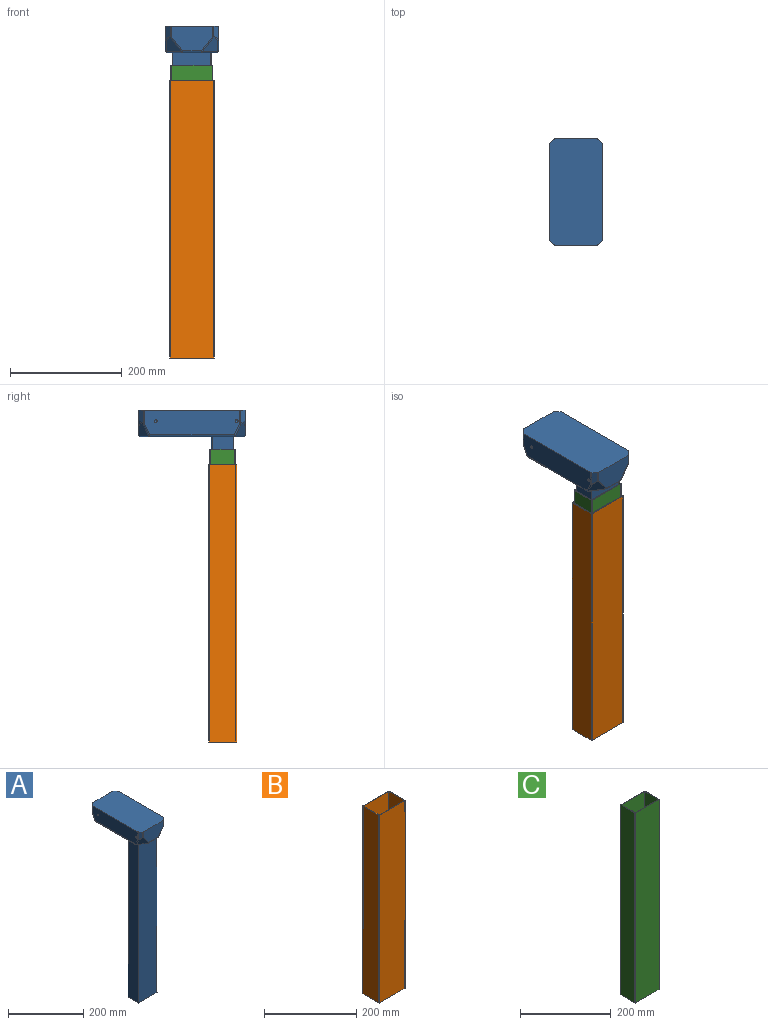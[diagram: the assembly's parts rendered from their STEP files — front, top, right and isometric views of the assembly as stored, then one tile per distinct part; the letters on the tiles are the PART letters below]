
ASSEMBLY  parts=3 mates=2
PART A: 90 faces, bbox 95.3x190.5x569.1 mm
  f0: plane 521.49x67.79mm, normal (0,1,0), area 35353mm2, adj f1,f13,f14,f79
  f1: cylinder r=1.27mm len=521.49mm, axis (0,0,-1), area 1040.3mm2, adj f0,f2,f14,f79
  f2: plane 521.49x39.09mm, normal (-1,0,0), area 20385.3mm2, adj f1,f3,f14,f79
  f3: plane 521.49x69.06mm, normal (0,-1,0), area 36015.3mm2, adj f2,f4,f14,f79
  f4: cylinder r=1.27mm len=521.49mm, axis (0,0,-1), area 1040.3mm2, adj f3,f5,f14,f79
  f5: plane 521.49x37.82mm, normal (1,0,0), area 19723mm2, adj f4,f13,f14,f79
  f6: cylinder r=0.13mm len=521.49mm, axis (0,0,-1), area 104mm2, adj f7,f12,f14,f81
  f7: plane 521.49x66.93mm, normal (0,-1,0), area 34902.6mm2, adj f6,f8,f14,f81
  f8: cylinder r=0.13mm len=521.49mm, axis (0,0,-1), area 104mm2, adj f7,f9,f14,f81
  f9: plane 521.49x36.96mm, normal (-1,0,0), area 19272.6mm2, adj f8,f10,f14,f81
  f10: cylinder r=0.13mm len=521.49mm, axis (0,0,-1), area 104mm2, adj f9,f11,f14,f81
  f11: plane 521.49x67.06mm, normal (0,1,0), area 34968.9mm2, adj f10,f12,f14,f81
  f12: plane 521.49x37.08mm, normal (1,0,0), area 19338.8mm2, adj f6,f11,f14,f81
  f13: cylinder r=1.27mm len=521.49mm, axis (0,0,-1), area 1040.3mm2, adj f0,f5,f14,f79
  f14: plane 70.33x40.36mm, normal (0,0,-1), area 337.7mm2, adj f0,f1,f2,f3,f4,f5,f6,f7
  f15: sphere r=3.17mm, area 8.3mm2, adj f16,f17,f59
  f16: cylinder r=3.17mm len=28.98mm, axis (0.86,-0.51,0), area 121mm2, adj f15,f18,f25,f79
  f17: cylinder r=3.17mm len=21.77mm, axis (0,0.42,0.91), area 76mm2, adj f15,f19,f20,f25,f66
  f18: sphere r=3.17mm, area 4.4mm2, adj f16,f21,f73
  f19: bspline ~1.32x1.19mm, area 0.6mm2, adj f17,f20,f22
  f20: bspline ~1.92x1.25mm, area 1.6mm2, adj f17,f19,f61,f65
  f21: cylinder r=3.17mm len=27.64mm, axis (-0.61,0,-0.79), area 68.8mm2, adj f18,f23,f24,f25,f76
  f22: cylinder r=3.17mm len=8.09mm, axis (-0.6,0.6,0.52), area 17.1mm2, adj f19,f24,f25,f65
  f23: bspline ~1.81x0.76mm, area 0.7mm2, adj f21,f24,f60,f65
  f24: bspline ~1.61x1.55mm, area 1mm2, adj f21,f22,f23
  f25: plane 27.46x26.12mm, normal (0.48,0.8,-0.37), area 540.1mm2, adj f16,f17,f21,f22
  f26: bspline ~1.92x1.25mm, area 1.6mm2, adj f27,f28,f75,f77
  f27: bspline ~1.32x1.19mm, area 0.6mm2, adj f26,f28,f29
  f28: cylinder r=3.17mm len=21.77mm, axis (0,-0.42,-0.91), area 76mm2, adj f26,f27,f30,f36,f80
  f29: cylinder r=3.17mm len=8.09mm, axis (-0.6,-0.6,-0.52), area 17.1mm2, adj f27,f31,f36,f77
  f30: sphere r=3.17mm, area 8.3mm2, adj f28,f32,f78
  f31: bspline ~1.61x1.55mm, area 1mm2, adj f29,f33,f34
  f32: cylinder r=3.17mm len=28.98mm, axis (0.86,0.51,0), area 121mm2, adj f30,f35,f36,f79
  f33: bspline ~1.81x0.76mm, area 0.7mm2, adj f31,f34,f74,f77
  f34: cylinder r=3.17mm len=27.64mm, axis (-0.61,0,0.79), area 68.8mm2, adj f31,f33,f35,f36,f76
  f35: sphere r=3.17mm, area 4.4mm2, adj f32,f34,f73
  f36: plane 27.46x26.12mm, normal (-0.48,0.8,-0.37), area 540.1mm2, adj f28,f29,f32,f34
  f37: bspline ~1.81x0.76mm, area 0.7mm2, adj f38,f39,f69,f72
  f38: bspline ~1.61x1.55mm, area 1mm2, adj f37,f39,f40
  f39: cylinder r=3.17mm len=27.64mm, axis (0.61,0,-0.79), area 68.8mm2, adj f37,f38,f41,f47,f71
  f40: cylinder r=3.17mm len=8.09mm, axis (0.6,-0.6,0.52), area 17.1mm2, adj f38,f42,f47,f72
  f41: sphere r=3.17mm, area 4.4mm2, adj f39,f43,f68
  f42: bspline ~1.32x1.19mm, area 0.6mm2, adj f40,f44,f45
  f43: cylinder r=3.17mm len=28.98mm, axis (-0.86,0.51,0), area 121mm2, adj f41,f46,f47,f79
  f44: bspline ~1.92x1.25mm, area 1.6mm2, adj f42,f45,f70,f72
  f45: cylinder r=3.17mm len=21.77mm, axis (0,-0.42,0.91), area 76mm2, adj f42,f44,f46,f47,f80
  f46: sphere r=3.17mm, area 8.3mm2, adj f43,f45,f78
  f47: plane 27.46x26.12mm, normal (-0.48,-0.8,-0.37), area 540.1mm2, adj f39,f40,f43,f45
  f48: sphere r=3.17mm, area 4.4mm2, adj f49,f50,f68
  f49: cylinder r=3.17mm len=28.98mm, axis (-0.86,-0.51,0), area 121mm2, adj f48,f51,f58,f79
  f50: cylinder r=3.17mm len=27.64mm, axis (0.61,0,0.79), area 68.8mm2, adj f48,f52,f53,f58,f71
  f51: sphere r=3.17mm, area 8.3mm2, adj f49,f54,f59
  f52: bspline ~1.61x1.55mm, area 1mm2, adj f50,f53,f55
  f53: bspline ~1.81x0.76mm, area 0.7mm2, adj f50,f52,f63,f67
  f54: cylinder r=3.17mm len=21.77mm, axis (0,0.42,-0.91), area 76mm2, adj f51,f56,f57,f58,f66
  f55: cylinder r=3.17mm len=8.09mm, axis (0.6,0.6,-0.52), area 17.1mm2, adj f52,f57,f58,f67
  f56: bspline ~1.92x1.25mm, area 1.6mm2, adj f54,f57,f62,f67
  f57: bspline ~1.32x1.19mm, area 0.6mm2, adj f54,f55,f56
  f58: plane 27.46x26.12mm, normal (0.48,-0.8,-0.37), area 540.1mm2, adj f49,f50,f54,f55
  f59: cylinder r=3.17mm len=151.2mm, axis (0,1,0), area 754.1mm2, adj f15,f51,f66,f79
  f60: cylinder r=2.54mm len=17.99mm, axis (0,0,-1), area 35.9mm2, adj f23,f64,f65,f76
  f61: cylinder r=2.54mm len=23.86mm, axis (0,0,-1), area 47.6mm2, adj f20,f64,f65,f66
  f62: cylinder r=2.54mm len=23.86mm, axis (0,0,-1), area 47.6mm2, adj f56,f64,f66,f67
  f63: cylinder r=2.54mm len=17.99mm, axis (0,0,1), area 35.9mm2, adj f53,f64,f67,f71
  f64: plane 190.5x95.25mm, normal (0,0,1), area 17982.7mm2, adj f60,f61,f62,f63,f65,f66,f67,f69
  f65: plane 24.48x7.49mm, normal (0.71,0.71,0), area 226.5mm2, adj f20,f22,f23,f60,f61,f64
  f66: plane 170.44x44.45mm, normal (1,0,0), area 7338.6mm2, adj f17,f54,f59,f61,f62,f64,f87,f89
  f67: plane 24.48x7.49mm, normal (0.71,-0.71,0), area 226.5mm2, adj f53,f55,f56,f62,f63,f64
  f68: cylinder r=3.17mm len=33.98mm, axis (1,0,0), area 169.5mm2, adj f41,f48,f71,f79
  f69: cylinder r=2.54mm len=17.99mm, axis (0,0,-1), area 35.9mm2, adj f37,f64,f71,f72
  f70: cylinder r=2.54mm len=23.86mm, axis (0,0,-1), area 47.6mm2, adj f44,f64,f72,f80
  f71: plane 75.19x44.45mm, normal (0,-1,0), area 2796.9mm2, adj f39,f50,f63,f64,f68,f69
  f72: plane 24.48x7.49mm, normal (-0.71,-0.71,0), area 226.5mm2, adj f37,f40,f44,f64,f69,f70
  f73: cylinder r=3.17mm len=33.98mm, axis (-1,0,0), area 169.5mm2, adj f18,f35,f76,f79
  f74: cylinder r=2.54mm len=17.99mm, axis (0,0,-1), area 35.9mm2, adj f33,f64,f76,f77
  f75: cylinder r=2.54mm len=23.86mm, axis (0,0,1), area 47.6mm2, adj f26,f64,f77,f80
  f76: plane 75.19x44.45mm, normal (0,1,0), area 2796.9mm2, adj f21,f34,f60,f64,f73,f74
  f77: plane 24.48x7.49mm, normal (-0.71,0.71,0), area 226.5mm2, adj f26,f29,f33,f64,f74,f75
  f78: cylinder r=3.17mm len=151.2mm, axis (0,-1,0), area 754.1mm2, adj f30,f46,f79,f80
  f79: plane 184.15x88.9mm, normal (0,0,-1), area 12628.5mm2, adj f0,f1,f2,f3,f4,f5,f13,f16
  f80: plane 170.44x44.45mm, normal (-1,0,0), area 7338.6mm2, adj f28,f45,f64,f70,f75,f78,f83,f85
  f81: plane 67.18x37.21mm, normal (0,0,-1), area 2499.9mm2, adj f6,f7,f8,f9,f10,f11,f12
  f82: cone r=0mm half-angle=59deg, axis (-1,0,0), area 22.9mm2, adj f83
  f83: cylinder r=2.5mm len=15.7mm, axis (-1,0,0), area 246.6mm2, adj f80,f82
  f84: cone r=0mm half-angle=59deg, axis (-1,0,0), area 22.9mm2, adj f85
  f85: cylinder r=2.5mm len=15.7mm, axis (-1,0,0), area 246.6mm2, adj f80,f84
  f86: cone r=0mm half-angle=59deg, axis (1,0,0), area 22.9mm2, adj f87
  f87: cylinder r=2.5mm len=15.7mm, axis (1,0,0), area 246.6mm2, adj f66,f86
  f88: cone r=0mm half-angle=59deg, axis (1,0,0), area 22.9mm2, adj f89
  f89: cylinder r=2.5mm len=15.7mm, axis (1,0,0), area 246.6mm2, adj f66,f88
PART B: 18 faces, bbox 80.3x50.4x496.9 mm
  f0: plane 496.9x47.88mm, normal (-1,0,0), area 23791.1mm2, adj f1,f15,f16,f17
  f1: cylinder r=1.27mm len=496.9mm, axis (0,0,-1), area 991.3mm2, adj f0,f2,f16,f17
  f2: plane 496.9x77.78mm, normal (0,-1,0), area 38646.3mm2, adj f1,f3,f16,f17
  f3: cylinder r=1.27mm len=496.9mm, axis (0,0,-1), area 991.3mm2, adj f2,f4,f16,f17
  f4: plane 496.9x47.88mm, normal (1,0,0), area 23791.1mm2, adj f3,f5,f16,f17
  f5: cylinder r=1.27mm len=496.9mm, axis (0,0,-1), area 991.3mm2, adj f4,f6,f16,f17
  f6: plane 496.9x77.78mm, normal (0,1,0), area 38646.3mm2, adj f5,f15,f16,f17
  f7: cylinder r=0.13mm len=496.9mm, axis (0,0,-1), area 99.1mm2, adj f8,f14,f16,f17
  f8: plane 496.9x47.02mm, normal (1,0,0), area 23362mm2, adj f7,f9,f16,f17
  f9: cylinder r=0.13mm len=496.9mm, axis (0,0,-1), area 99.1mm2, adj f8,f10,f16,f17
  f10: plane 496.9x76.91mm, normal (0,-1,0), area 38217.2mm2, adj f9,f11,f16,f17
  f11: cylinder r=0.13mm len=496.9mm, axis (0,0,-1), area 99.1mm2, adj f10,f12,f16,f17
  f12: plane 496.9x47.02mm, normal (-1,0,0), area 23362mm2, adj f11,f13,f16,f17
  f13: cylinder r=0.13mm len=496.9mm, axis (0,0,-1), area 99.1mm2, adj f12,f14,f16,f17
  f14: plane 496.9x76.91mm, normal (0,1,0), area 38217.2mm2, adj f7,f13,f16,f17
  f15: cylinder r=1.27mm len=496.9mm, axis (0,0,-1), area 991.3mm2, adj f0,f6,f16,f17
  f16: plane 80.32x50.42mm, normal (0,0,1), area 400.5mm2, adj f0,f1,f2,f3,f4,f5,f6,f7
  f17: plane 80.32x50.42mm, normal (0,0,-1), area 400.5mm2, adj f0,f1,f2,f3,f4,f5,f6,f7
PART C: 18 faces, bbox 75.2x45.4x511.2 mm
  f0: plane 511.18x42.9mm, normal (-1,0,0), area 21929.7mm2, adj f1,f15,f16,f17
  f1: cylinder r=1.27mm len=511.18mm, axis (0,0,-1), area 1019.7mm2, adj f0,f2,f16,f17
  f2: plane 511.18x72.7mm, normal (0,-1,0), area 37159.8mm2, adj f1,f3,f16,f17
  f3: cylinder r=1.27mm len=511.18mm, axis (0,0,-1), area 1019.7mm2, adj f2,f4,f16,f17
  f4: plane 511.18x42.9mm, normal (1,0,0), area 21929.7mm2, adj f3,f5,f16,f17
  f5: cylinder r=1.27mm len=511.18mm, axis (0,0,-1), area 1019.7mm2, adj f4,f6,f16,f17
  f6: plane 511.18x72.7mm, normal (0,1,0), area 37159.8mm2, adj f5,f15,f16,f17
  f7: cylinder r=0.13mm len=511.18mm, axis (0,0,-1), area 102mm2, adj f8,f14,f16,f17
  f8: plane 511.18x42.04mm, normal (1,0,0), area 21488.3mm2, adj f7,f9,f16,f17
  f9: cylinder r=0.13mm len=511.18mm, axis (0,0,-1), area 102mm2, adj f8,f10,f16,f17
  f10: plane 511.18x71.83mm, normal (0,-1,0), area 36718.3mm2, adj f9,f11,f16,f17
  f11: cylinder r=0.13mm len=511.18mm, axis (0,0,-1), area 102mm2, adj f10,f12,f16,f17
  f12: plane 511.18x42.04mm, normal (-1,0,0), area 21488.3mm2, adj f11,f13,f16,f17
  f13: cylinder r=0.13mm len=511.18mm, axis (0,0,-1), area 102mm2, adj f12,f14,f16,f17
  f14: plane 511.18x71.83mm, normal (0,1,0), area 36718.3mm2, adj f7,f13,f16,f17
  f15: cylinder r=1.27mm len=511.18mm, axis (0,0,-1), area 1019.7mm2, adj f0,f6,f16,f17
  f16: plane 75.24x45.44mm, normal (0,0,1), area 368.8mm2, adj f0,f1,f2,f3,f4,f5,f6,f7
  f17: plane 75.24x45.44mm, normal (0,0,-1), area 368.8mm2, adj f0,f1,f2,f3,f4,f5,f6,f7
PLACE A t=(0.04,0.02,25.4)mm
PLACE B at identity fixed
PLACE C t=(0,0,12.7)mm
MATE slider A.f14 <-> B.f17  axis (0,0,1) through (0,0,25.4)mm
MATE slider C.f17 <-> B.f17  axis (0,0,1) through (0,0,12.7)mm
